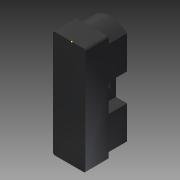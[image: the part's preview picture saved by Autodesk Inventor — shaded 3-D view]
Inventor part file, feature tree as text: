
AUTODESK INVENTOR PART (.ipt)
format: ipt  version: 2015 (Build 190159000, 159)  size: 176,640 bytes
history: native  units: mm
features: sketch x5, extrude x4, mirror x4, plane x2, fillet x1, shell x1
ambient origin geometry x8: Origin, YZ Plane, XZ Plane, XY Plane, X Axis, Y Axis, Z Axis, Center Point
bodies: Solid1 (feature_tree)
feature tree (17):
  extrude  "Extrusion1"  Depth=17.6mm
  plane  "Work Plane1"
  fillet  "Fillet1"  Radius=22.5mm
  mirror  "Mirror1"
  plane  "Work Plane2"
  mirror  "Mirror2"
  extrude  "Extrusion3"  Depth=15.0mm
  sketch  "Sketch3"  dims[d6=10.1mm d7=21.5mm]
  extrude  "Extrusion4"  Depth=21.5mm
  extrude  "Extrusion5"  Depth=10.0mm TaperAngle=0.0deg
  mirror  "Mirror3"
  mirror  "Mirror4"
  shell  "Shell1"  Thickness=4.2mm
  sketch  "Sketch1"  dims[d0=58.0mm d1=17.6mm d2=22.5mm d3=0.0mm]
  sketch  "Sketch2"  dims[d4=1.0mm d5=15.0mm]
  sketch  "Sketch4"  dims[d10=1.5mm d11=10.0mm d12=0.0mm d13=4.2mm]
  sketch  "Sketch9"  dims[d14=5.0mm d15=7.5mm d16=1.5mm d17=0.0mm d20=25.0mm d21=8.8mm d22=10.0mm d23=0.0mm d24=1.0mm]
